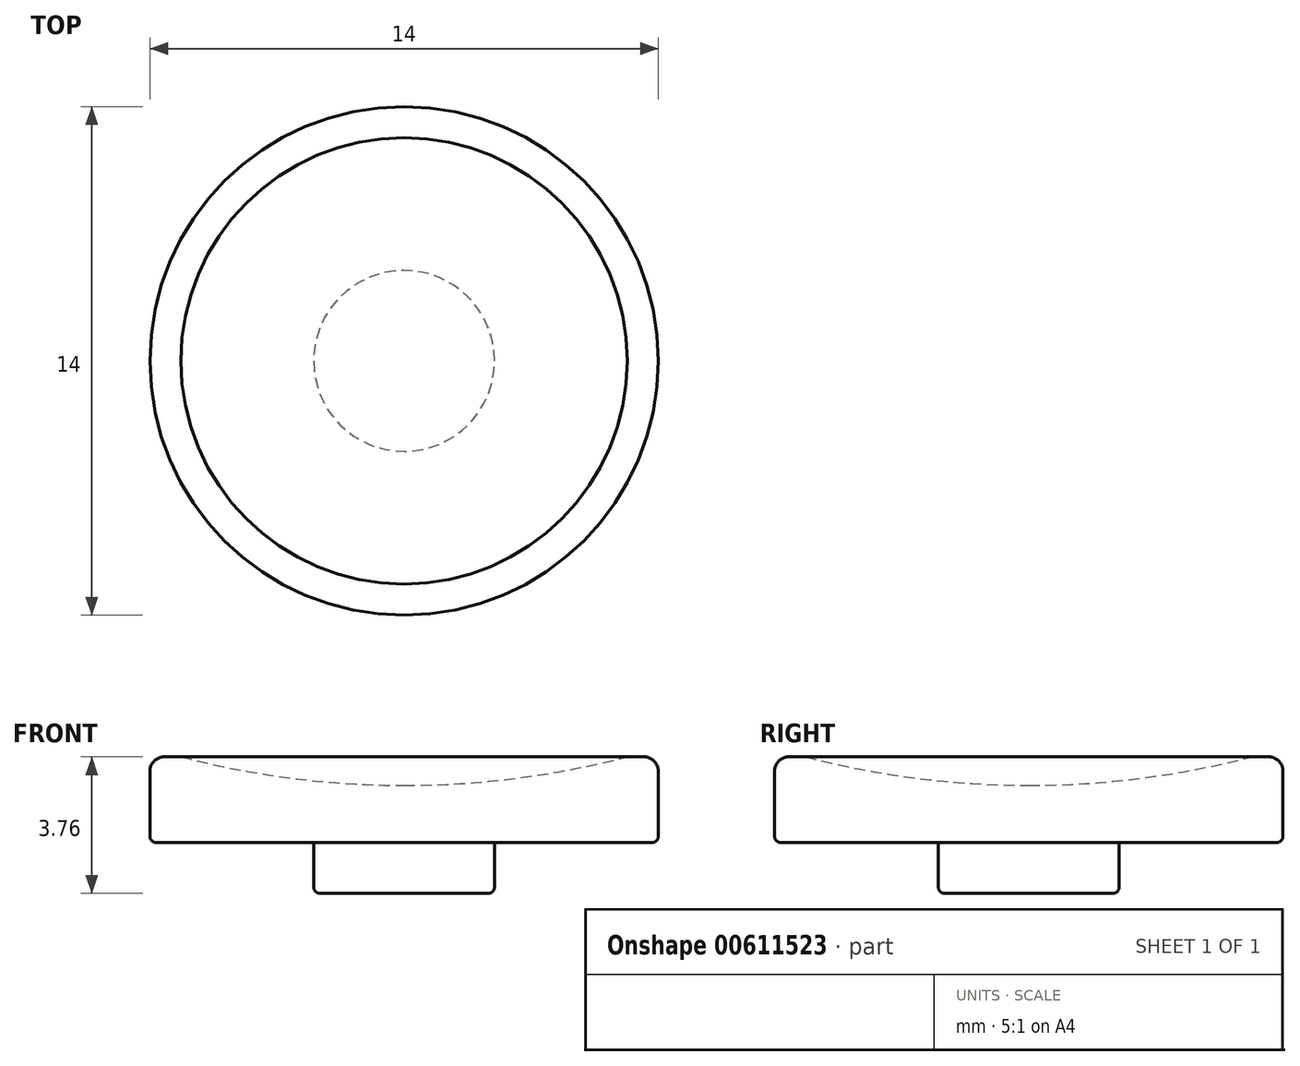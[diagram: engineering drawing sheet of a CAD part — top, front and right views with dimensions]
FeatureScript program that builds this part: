
annotation { "Feature Type Name" : "Feature", "Feature Type Description" : "" }
export const myFeature = defineFeature(function(context is Context, id is Id, definition is map)
    precondition{}
    {
        {
            var Q0;
            Q0=qCreatedBy(makeId("Front.planeOp"),FACE);
            var sketch = newSketch(context, id + "F0", { "sketchPlane" : qUnion([Q0])});
            skLineSegment(sketch, "E0.bottom", {"start": v(0, 0) * mm, "end": v(-7, 0) * mm});
            skLineSegment(sketch, "E0.left", {"start": v(0, 0) * mm, "end": v(0, 1.57) * mm});
            skLineSegment(sketch, "E0.right", {"start": v(-7, 0) * mm, "end": v(-7, 2.36) * mm});
            skArc(sketch, "E1", {"start": v(-6.14, 2.36) * mm, "mid": v(-3.1, 1.77) * mm, "end": v(0, 1.57) * mm});
            skLineSegment(sketch, "E2", {"start": v(-7, 2.36) * mm, "end": v(-6.14, 2.36) * mm});
            skSolve(sketch);
        }
        {
            var Q0;
            Q0=makeQuery(id+"F0.imprint","IMPRINT",FACE,{"disambiguationData":[TD([[makeQuery(id+"F0.imprint","IMPRINT",EDGE,{"derivedFrom":sQuery(id+"F0.wireOp",EDGE,"E0.bottom")}),-1.0]])]});
            var Q1;
            Q1=sQuery(id+"F0.wireOp",EDGE,"E0.left");
            revolve(context, id + "F1", {"entities" : qUnion([Q0]), "axis" : qUnion([Q1]), "revolveType" : RevolveType.FULL});
        }
        {
            var Q0;
            Q0=makeQuery(id+"F1.opRevolve","SWEPT_EDGE",EDGE,{"disambiguationData":[OSD([sQuery(id+"F0.wireOp",EDGE,"E0.right"),sQuery(id+"F0.wireOp",EDGE,"E2")])]});
            fillet(context, id + "F2", {"entities" : qUnion([Q0]), "radius" : .4 * mm, "tangentPropagation" : true, "allowEdgeOverflow" : false});
        }
        {
            var Q0;
            Q0=makeQuery(id+"F1.opRevolve","SWEPT_FACE",FACE,{"disambiguationData":[OSD([sQuery(id+"F0.wireOp",EDGE,"E0.bottom")])]});
            var sketch = newSketch(context, id + "F3", { "sketchPlane" : qUnion([Q0])});
            skCircle(sketch, "E3", {"center": v(0, 0) * mm, "radius": 2.5 * mm});
            skSolve(sketch);
        }
        {
            var Q0;
            Q0 = qSketchRegion(id + "F3", true);
            extrude(context, id + "F4", {"entities" : qUnion([Q0]), "operationType" : NewBodyOperationType.ADD, "depth" : 1.4 * mm, "offsetDistance" : 25 * mm});
        }
        {
            var Q0;
            Q0=makeQuery(id+"F4.opExtrude","CAP_FACE",FACE,{"disambiguationData":[OSD([sQuery(id+"F3.wireOp",EDGE,"E3")])],"isStart":false});
            var Q1;
            Q1=makeQuery(id+"F4.opExtrude","CAP_EDGE",EDGE,{"disambiguationData":[OSD([sQuery(id+"F3.wireOp",EDGE,"E3")])],"isStart":true});
            var Q2;
            Q2=makeQuery(id+"F1.opRevolve","SWEPT_EDGE",EDGE,{"disambiguationData":[OSD([sQuery(id+"F0.wireOp",EDGE,"E0.bottom"),sQuery(id+"F0.wireOp",EDGE,"E0.right")])]});
            fillet(context, id + "F5", {"entities" : qUnion([Q0, Q1, Q2]), "radius" : .175 * mm, "tangentPropagation" : true, "allowEdgeOverflow" : false});
        }
    });
